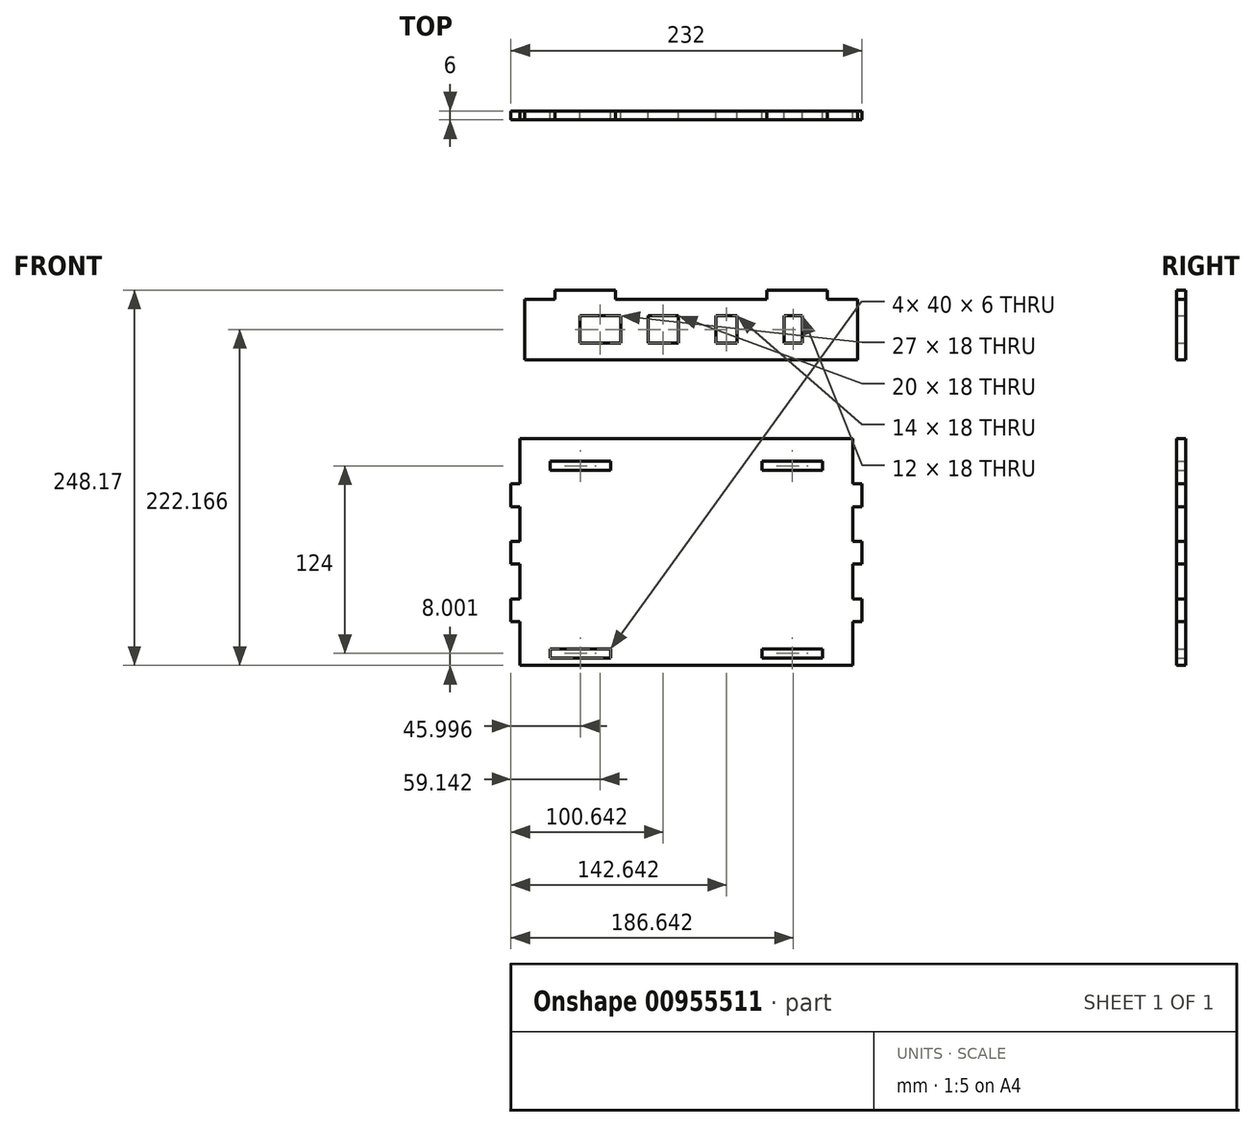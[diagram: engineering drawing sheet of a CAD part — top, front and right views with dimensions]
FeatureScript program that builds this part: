
annotation { "Feature Type Name" : "Feature", "Feature Type Description" : "" }
export const myFeature = defineFeature(function(context is Context, id is Id, definition is map)
    precondition{}
    {
        {
            var Q0;
            Q0=qCreatedBy(makeId("Front.planeOp"),FACE);
            var sketch = newSketch(context, id + "F0", { "sketchPlane" : qUnion([Q0])});
            skLineSegment(sketch, "E0.bottom", {"start": v(-42.3, 41.62) * mm, "end": v(-15.3, 41.62) * mm});
            skLineSegment(sketch, "E0.top", {"start": v(-42.3, 23.62) * mm, "end": v(-15.3, 23.62) * mm});
            skLineSegment(sketch, "E0.left", {"start": v(-42.3, 41.62) * mm, "end": v(-42.3, 23.62) * mm});
            skLineSegment(sketch, "E0.right", {"start": v(-15.3, 41.62) * mm, "end": v(-15.3, 23.62) * mm});
            skLineSegment(sketch, "E1.bottom", {"start": v(2.7, 41.62) * mm, "end": v(22.7, 41.62) * mm});
            skLineSegment(sketch, "E1.top", {"start": v(2.7, 23.62) * mm, "end": v(22.7, 23.62) * mm});
            skLineSegment(sketch, "E1.left", {"start": v(2.7, 41.62) * mm, "end": v(2.7, 23.62) * mm});
            skLineSegment(sketch, "E1.right", {"start": v(22.7, 41.62) * mm, "end": v(22.7, 23.62) * mm});
            skLineSegment(sketch, "E2.bottom", {"start": v(47.7, 41.62) * mm, "end": v(61.7, 41.62) * mm});
            skLineSegment(sketch, "E2.top", {"start": v(47.7, 23.62) * mm, "end": v(61.7, 23.62) * mm});
            skLineSegment(sketch, "E2.left", {"start": v(47.7, 41.62) * mm, "end": v(47.7, 23.62) * mm});
            skLineSegment(sketch, "E2.right", {"start": v(61.7, 41.62) * mm, "end": v(61.7, 23.62) * mm});
            skLineSegment(sketch, "E3.bottom", {"start": v(92.7, 41.62) * mm, "end": v(104.7, 41.62) * mm});
            skLineSegment(sketch, "E3.top", {"start": v(92.7, 23.62) * mm, "end": v(104.7, 23.62) * mm});
            skLineSegment(sketch, "E3.left", {"start": v(92.7, 41.62) * mm, "end": v(92.7, 23.62) * mm});
            skLineSegment(sketch, "E3.right", {"start": v(104.7, 41.62) * mm, "end": v(104.7, 23.62) * mm});
            skLineSegment(sketch, "E4.bottom", {"start": v(-78.8, 52.62) * mm, "end": v(-58.8, 52.62) * mm});
            skLineSegment(sketch, "E4.top", {"start": v(-78.8, 12.62) * mm, "end": v(141.2, 12.62) * mm});
            skLineSegment(sketch, "E4.left", {"start": v(-78.8, 52.62) * mm, "end": v(-78.8, 12.62) * mm});
            skLineSegment(sketch, "E4.right", {"start": v(141.2, 52.62) * mm, "end": v(141.2, 12.62) * mm});
            skLineSegment(sketch, "E5.bottom", {"start": v(-81.94, -39.55) * mm, "end": v(138.06, -39.55) * mm});
            skLineSegment(sketch, "E5.top", {"start": v(-81.94, -189.55) * mm, "end": v(138.06, -189.55) * mm});
            skLineSegment(sketch, "E5.left", {"start": v(-81.94, -39.55) * mm, "end": v(-81.94, -69.55) * mm});
            skLineSegment(sketch, "E5.right", {"start": v(138.06, -39.55) * mm, "end": v(138.06, -69.55) * mm});
            skLineSegment(sketch, "E6", {"start": v(-78.8, 32.62) * mm, "end": v(141.2, 32.62) * mm, "construction": true});
            skPoint(sketch, "E7", {"position": v(-42.3, 32.62) * mm});
            skLineSegment(sketch, "E8.top", {"start": v(-58.8, 58.62) * mm, "end": v(-18.8, 58.62) * mm});
            skLineSegment(sketch, "E8.left", {"start": v(-58.8, 52.62) * mm, "end": v(-58.8, 58.62) * mm});
            skLineSegment(sketch, "E8.right", {"start": v(-18.8, 52.62) * mm, "end": v(-18.8, 58.62) * mm});
            skLineSegment(sketch, "E9.top", {"start": v(81.2, 58.62) * mm, "end": v(121.2, 58.62) * mm});
            skLineSegment(sketch, "E9.left", {"start": v(81.2, 52.62) * mm, "end": v(81.2, 58.62) * mm});
            skLineSegment(sketch, "E9.right", {"start": v(121.2, 52.62) * mm, "end": v(121.2, 58.62) * mm});
            skLineSegment(sketch, "E10", {"start": v(-81.94, -54.55) * mm, "end": v(138.06, -54.55) * mm, "construction": true});
            skLineSegment(sketch, "E11", {"start": v(-81.94, -184.55) * mm, "end": v(138.06, -184.55) * mm, "construction": true});
            skLineSegment(sketch, "E12.bottom", {"start": v(-81.94, -69.55) * mm, "end": v(-87.94, -69.55) * mm});
            skLineSegment(sketch, "E12.top", {"start": v(-81.94, -84.55) * mm, "end": v(-87.94, -84.55) * mm});
            skLineSegment(sketch, "E12.right", {"start": v(-87.94, -69.55) * mm, "end": v(-87.94, -84.55) * mm});
            skLineSegment(sketch, "E13.0.1.0", {"start": v(-81.94, -107.55) * mm, "end": v(-87.94, -107.55) * mm});
            skLineSegment(sketch, "E13.0.1.1", {"start": v(-87.94, -107.55) * mm, "end": v(-87.94, -122.55) * mm});
            skLineSegment(sketch, "E13.0.1.2", {"start": v(-81.94, -122.55) * mm, "end": v(-87.94, -122.55) * mm});
            skLineSegment(sketch, "E13.0.2.0", {"start": v(-81.94, -145.55) * mm, "end": v(-87.94, -145.55) * mm});
            skLineSegment(sketch, "E13.0.2.1", {"start": v(-87.94, -145.55) * mm, "end": v(-87.94, -160.55) * mm});
            skLineSegment(sketch, "E13.0.2.2", {"start": v(-81.94, -160.55) * mm, "end": v(-87.94, -160.55) * mm});
            skLineSegment(sketch, "E13.1.0.0", {"start": v(144.06, -69.55) * mm, "end": v(138.06, -69.55) * mm});
            skLineSegment(sketch, "E13.1.0.2", {"start": v(144.06, -84.55) * mm, "end": v(138.06, -84.55) * mm});
            skLineSegment(sketch, "E13.1.0.3", {"start": v(144.06, -69.55) * mm, "end": v(144.06, -84.55) * mm});
            skLineSegment(sketch, "E13.1.1.0", {"start": v(144.06, -107.55) * mm, "end": v(138.06, -107.55) * mm});
            skLineSegment(sketch, "E13.1.1.2", {"start": v(144.06, -122.55) * mm, "end": v(138.06, -122.55) * mm});
            skLineSegment(sketch, "E13.1.1.3", {"start": v(144.06, -107.55) * mm, "end": v(144.06, -122.55) * mm});
            skLineSegment(sketch, "E13.1.2.0", {"start": v(144.06, -145.55) * mm, "end": v(138.06, -145.55) * mm});
            skLineSegment(sketch, "E13.1.2.2", {"start": v(144.06, -160.55) * mm, "end": v(138.06, -160.55) * mm});
            skLineSegment(sketch, "E13.1.2.3", {"start": v(144.06, -145.55) * mm, "end": v(144.06, -160.55) * mm});
            skLineSegment(sketch, "E13.direction1", {"start": v(-87.94, -69.55) * mm, "end": v(138.06, -69.55) * mm, "construction": true});
            skLineSegment(sketch, "E13.direction2", {"start": v(-87.94, -69.55) * mm, "end": v(-87.94, -107.55) * mm, "construction": true});
            skLineSegment(sketch, "E14.bottom", {"start": v(-61.94, -184.55) * mm, "end": v(-21.94, -184.55) * mm});
            skLineSegment(sketch, "E14.top", {"start": v(-61.94, -178.55) * mm, "end": v(-21.94, -178.55) * mm});
            skLineSegment(sketch, "E14.left", {"start": v(-61.94, -184.55) * mm, "end": v(-61.94, -178.55) * mm});
            skLineSegment(sketch, "E14.right", {"start": v(-21.94, -184.55) * mm, "end": v(-21.94, -178.55) * mm});
            skLineSegment(sketch, "E15.bottom", {"start": v(118.06, -184.55) * mm, "end": v(78.06, -184.55) * mm});
            skLineSegment(sketch, "E15.top", {"start": v(118.06, -178.55) * mm, "end": v(78.06, -178.55) * mm});
            skLineSegment(sketch, "E15.left", {"start": v(118.06, -184.55) * mm, "end": v(118.06, -178.55) * mm});
            skLineSegment(sketch, "E15.right", {"start": v(78.06, -184.55) * mm, "end": v(78.06, -178.55) * mm});
            skLineSegment(sketch, "E16.0.1.0", {"start": v(-61.94, -54.55) * mm, "end": v(-21.94, -54.55) * mm});
            skLineSegment(sketch, "E16.0.1.1", {"start": v(-61.94, -60.55) * mm, "end": v(-21.94, -60.55) * mm});
            skLineSegment(sketch, "E16.0.1.2", {"start": v(118.06, -54.55) * mm, "end": v(78.06, -54.55) * mm});
            skLineSegment(sketch, "E16.0.1.3", {"start": v(-21.94, -60.55) * mm, "end": v(-21.94, -54.55) * mm});
            skLineSegment(sketch, "E16.0.1.4", {"start": v(-61.94, -60.55) * mm, "end": v(-61.94, -54.55) * mm});
            skLineSegment(sketch, "E16.0.1.5", {"start": v(118.06, -60.55) * mm, "end": v(78.06, -60.55) * mm});
            skLineSegment(sketch, "E16.0.1.6", {"start": v(118.06, -60.55) * mm, "end": v(118.06, -54.55) * mm});
            skLineSegment(sketch, "E16.0.1.7", {"start": v(78.06, -60.55) * mm, "end": v(78.06, -54.55) * mm});
            skLineSegment(sketch, "E16.direction1", {"start": v(-61.94, -184.55) * mm, "end": v(-36.94, -184.55) * mm, "construction": true});
            skLineSegment(sketch, "E16.direction2", {"start": v(-61.94, -184.55) * mm, "end": v(-61.94, -60.55) * mm, "construction": true});
            skLineSegment(sketch, "E17.trimOffspring", {"start": v(-18.8, 52.62) * mm, "end": v(81.2, 52.62) * mm});
            skLineSegment(sketch, "E18.trimOffspring", {"start": v(121.2, 52.62) * mm, "end": v(141.2, 52.62) * mm});
            skLineSegment(sketch, "E19.trimOffspring", {"start": v(138.06, -84.55) * mm, "end": v(138.06, -107.55) * mm});
            skLineSegment(sketch, "E20.trimOffspring", {"start": v(138.06, -122.55) * mm, "end": v(138.06, -145.55) * mm});
            skLineSegment(sketch, "E21.trimOffspring", {"start": v(-81.94, -84.55) * mm, "end": v(-81.94, -107.55) * mm});
            skLineSegment(sketch, "E22.trimOffspring", {"start": v(-81.94, -122.55) * mm, "end": v(-81.94, -145.55) * mm});
            skLineSegment(sketch, "E23.trimOffspring", {"start": v(-81.94, -160.55) * mm, "end": v(-81.94, -189.55) * mm});
            skLineSegment(sketch, "E24.trimOffspring", {"start": v(138.06, -160.55) * mm, "end": v(138.06, -189.55) * mm});
            skSolve(sketch);
        }
        {
            var Q0;
            {var subQ5=sQuery(id+"F0.wireOp",EDGE,"E5.bottom");Q0=makeQuery(id+"F0.imprint","IMPRINT",FACE,{"disambiguationData":[TD([[makeQuery(id+"F0.imprint","IMPRINT",EDGE,{"derivedFrom":subQ5}),-1.0]])]});}
            extrude(context, id + "F1", {"entities" : qUnion([Q0]), "depth" : 6 * mm, "offsetDistance" : 25 * mm});
        }
        {
            var Q0;
            Q0=makeQuery(id+"F0.imprint","IMPRINT",FACE,{"disambiguationData":[TD([[makeQuery(id+"F0.imprint","IMPRINT",EDGE,{"derivedFrom":sQuery(id+"F0.wireOp",EDGE,"E0.bottom")}),1.0]])]});
            extrude(context, id + "F2", {"entities" : qUnion([Q0]), "depth" : 6 * mm, "offsetDistance" : 25 * mm});
        }
    });
